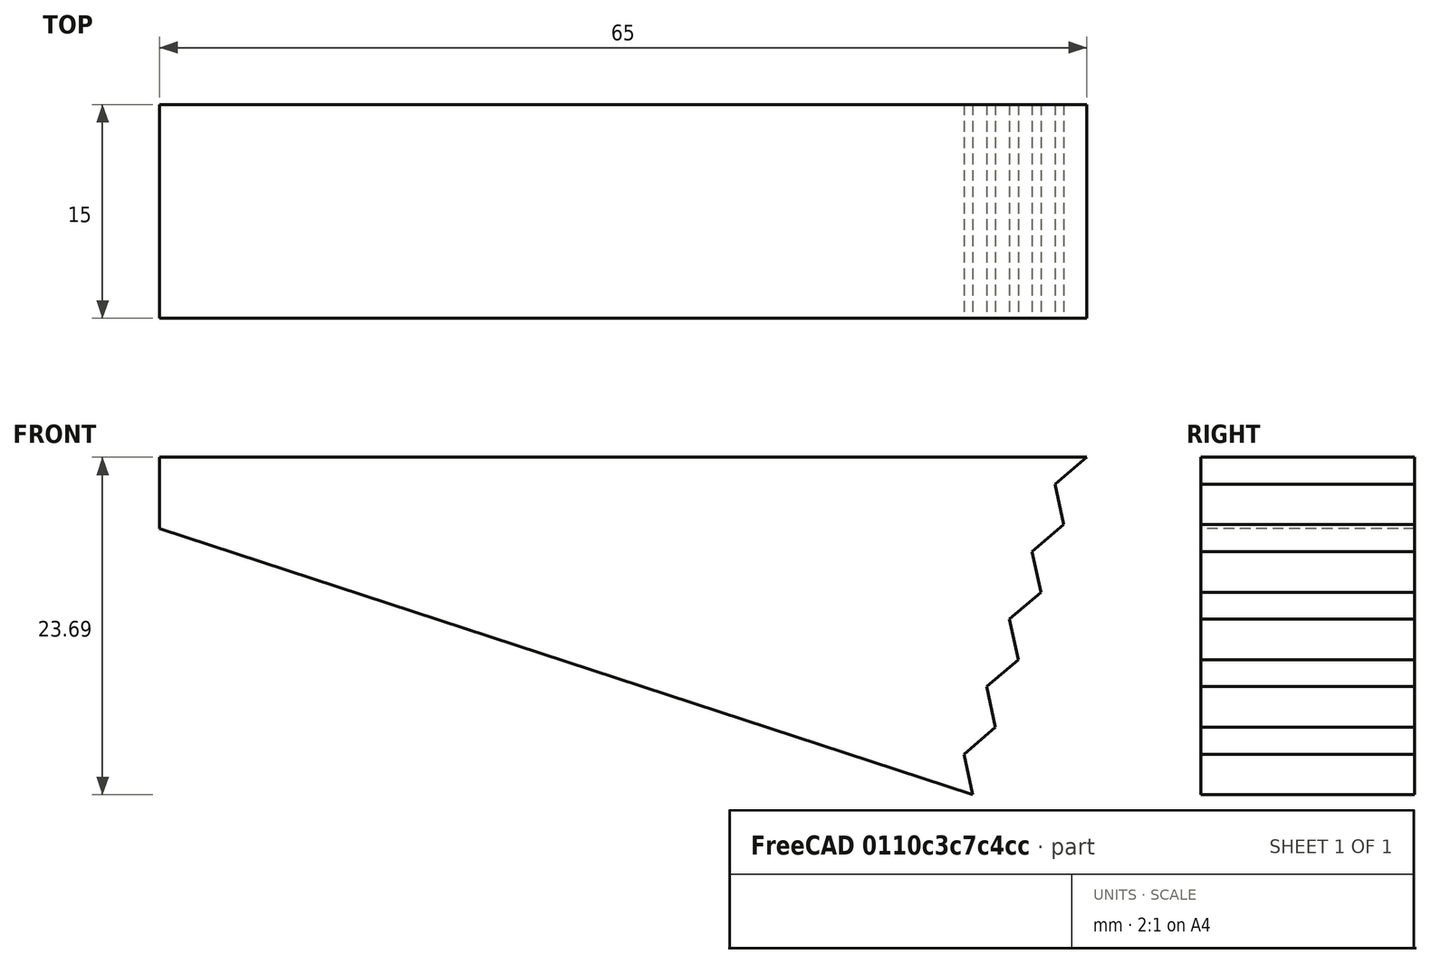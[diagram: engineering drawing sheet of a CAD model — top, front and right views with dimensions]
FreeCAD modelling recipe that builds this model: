
FCSTD DOCUMENT  (FreeCAD 0.21R33771 (Git))
Label: rbg_poc
License: All rights reserved
LicenseURL: https://en.wikipedia.org/wiki/All_rights_reserved
objects: Spreadsheet::Sheet×1, Sketcher::SketchObject×1, PartDesign::Pad×1, PartDesign::Body×1
note: 4 computed .brp shape members not serialized (recipe doc carries the construction recipe); baked Part::Feature solids carry a one-line shape summary decoded from their .brp

FEATURE [Spreadsheet::Sheet] Spreadsheet  label="measurements"
  cells = A1='max_band_length; B1(max_band_length)==70 mm; A2='shot_count; B2(shot_count)=5; A3='wall_thickness; B3(wall_thickness)==5 mm; A4='clip_tooth_width; B4(clip_tooth_width)==5 mm; A5='clip_tooth_depth; B5(clip_tooth_depth)==1.5 mm
FEATURE [Sketcher::SketchObject] Sketch
  FullyConstrained = true
  MapMode = 5
  Placement = pos=(0,0,0) rot=(1,0,0;1.5708rad)
  Support = -> [XZ_Plane]
  expr: .Constraints.clip_length = <<measurements>>.max_band_length - 5 mm
  expr: Constraints[36] = <<measurements>>.clip_tooth_width
  expr: Constraints[46] = <<measurements>>.clip_tooth_depth
  expr: Constraints[47] = .Constraints.clip_length - 5 mm
  sketch-geometry (18):
    g0: LineSegment StartX=0 StartY=0 StartZ=0 EndX=65 EndY=0 EndZ=0
    g1: LineSegment StartX=0 StartY=0 StartZ=0 EndX=0 EndY=-5 EndZ=0
    g2: LineSegment StartX=0 StartY=-5 StartZ=0 EndX=57.0146 EndY=-23.6904 EndZ=0
    g3: LineSegment StartX=65 StartY=0 StartZ=0 EndX=62.78 EndY=-1.88992 EndZ=0
    g4: LineSegment StartX=62.78 StartY=-1.88992 StartZ=0 EndX=63.4029 EndY=-4.73808 EndZ=0
    g5: LineSegment StartX=63.4029 StartY=-4.73808 StartZ=0 EndX=61.183 EndY=-6.62799 EndZ=0
    g6: LineSegment StartX=61.183 StartY=-6.62799 StartZ=0 EndX=61.8059 EndY=-9.47615 EndZ=0
    g7: LineSegment StartX=61.8059 StartY=-9.47615 StartZ=0 EndX=59.5859 EndY=-11.3661 EndZ=0
    g8: LineSegment StartX=59.5859 StartY=-11.3661 StartZ=0 EndX=60.2088 EndY=-14.2142 EndZ=0
    g9: LineSegment StartX=60.2088 StartY=-14.2142 StartZ=0 EndX=57.9888 EndY=-16.1041 EndZ=0
    g10: LineSegment StartX=57.9888 StartY=-16.1041 StartZ=0 EndX=58.6117 EndY=-18.9523 EndZ=0
    g11: LineSegment StartX=58.6117 StartY=-18.9523 StartZ=0 EndX=56.3918 EndY=-20.8422 EndZ=0
    g12: LineSegment StartX=56.3918 StartY=-20.8422 StartZ=0 EndX=57.0146 EndY=-23.6904 EndZ=0
    g13: LineSegment StartX=65 StartY=0 StartZ=0 EndX=63.4029 EndY=-4.73808 EndZ=0
    g14: LineSegment StartX=63.4029 StartY=-4.73808 StartZ=0 EndX=61.8059 EndY=-9.47615 EndZ=0
    g15: LineSegment StartX=61.8059 StartY=-9.47615 StartZ=0 EndX=60.2088 EndY=-14.2142 EndZ=0
    g16: LineSegment StartX=58.6117 StartY=-18.9523 StartZ=0 EndX=60.2088 EndY=-14.2142 EndZ=0
    g17: LineSegment StartX=58.6117 StartY=-18.9523 StartZ=0 EndX=57.0146 EndY=-23.6904 EndZ=0
  constraints (48):
    c: Horizontal(g0)
    c: Coincident(g1,g0)
    c: Vertical(g1)
    c: Coincident(g2,g1)
    c: Distance(g1) = 5
    c: Distance(g0) = 65  'clip_length'
    c: Coincident(g-1,g0)
    c: Coincident(g3,g0)
    c: Coincident(g4,g3)
    c: Coincident(g5,g4)
    c: Coincident(g7,g6)
    c: Coincident(g8,g7)
    c: Coincident(g11,g10)
    c: Coincident(g12,g11)
    c: Coincident(g12,g2)
    c: Coincident(g9,g8)
    c: Coincident(g6,g5)
    c: Coincident(g10,g9)
    c: Coincident(g13,g0)
    c: Coincident(g13,g4)
    c: Coincident(g14,g4)
    c: Coincident(g14,g6)
    c: Coincident(g15,g6)
    c: Coincident(g15,g8)
    c: Coincident(g16,g10)
    c: Coincident(g16,g8)
    c: Coincident(g17,g10)
    c: Coincident(g17,g2)
    c: Parallel(g13,g14)
    c: Parallel(g14,g15)
    c: Parallel(g15,g16)
    c: Parallel(g16,g17)
    c: Equal(g13,g14)
    c: Equal(g14,g15)
    c: Equal(g15,g16)
    c: Equal(g16,g17)
    c: Distance(g13) = 5
    c: Equal(g3,g4)
    c: Equal(g5,g4)
    c: Equal(g6,g5)
    c: Equal(g6,g7)
    c: Equal(g7,g8)
    c: Equal(g8,g9)
    c: Equal(g9,g10)
    c: Equal(g10,g11)
    c: Equal(g11,g12)
    c: Distance(g3,g13) = 1.5
    c: Distance(g2) = 60
FEATURE [PartDesign::Pad] Pad
  Direction = (0,-1,2e-16)
  Length = 15
  Length2 = 10
  Placement = pos=(0,0,0) rot=(1,0,0;1.5708rad)
  Profile = -> Sketch
  ReferenceAxis = -> Sketch [N_Axis]
  Type = 0
  expr: Length = 3 * <<measurements>>.wall_thickness
FEATURE [PartDesign::Body] Body
  Group = -> [Sketch,Pad]
  Origin = -> Origin
  Tip = -> Pad
